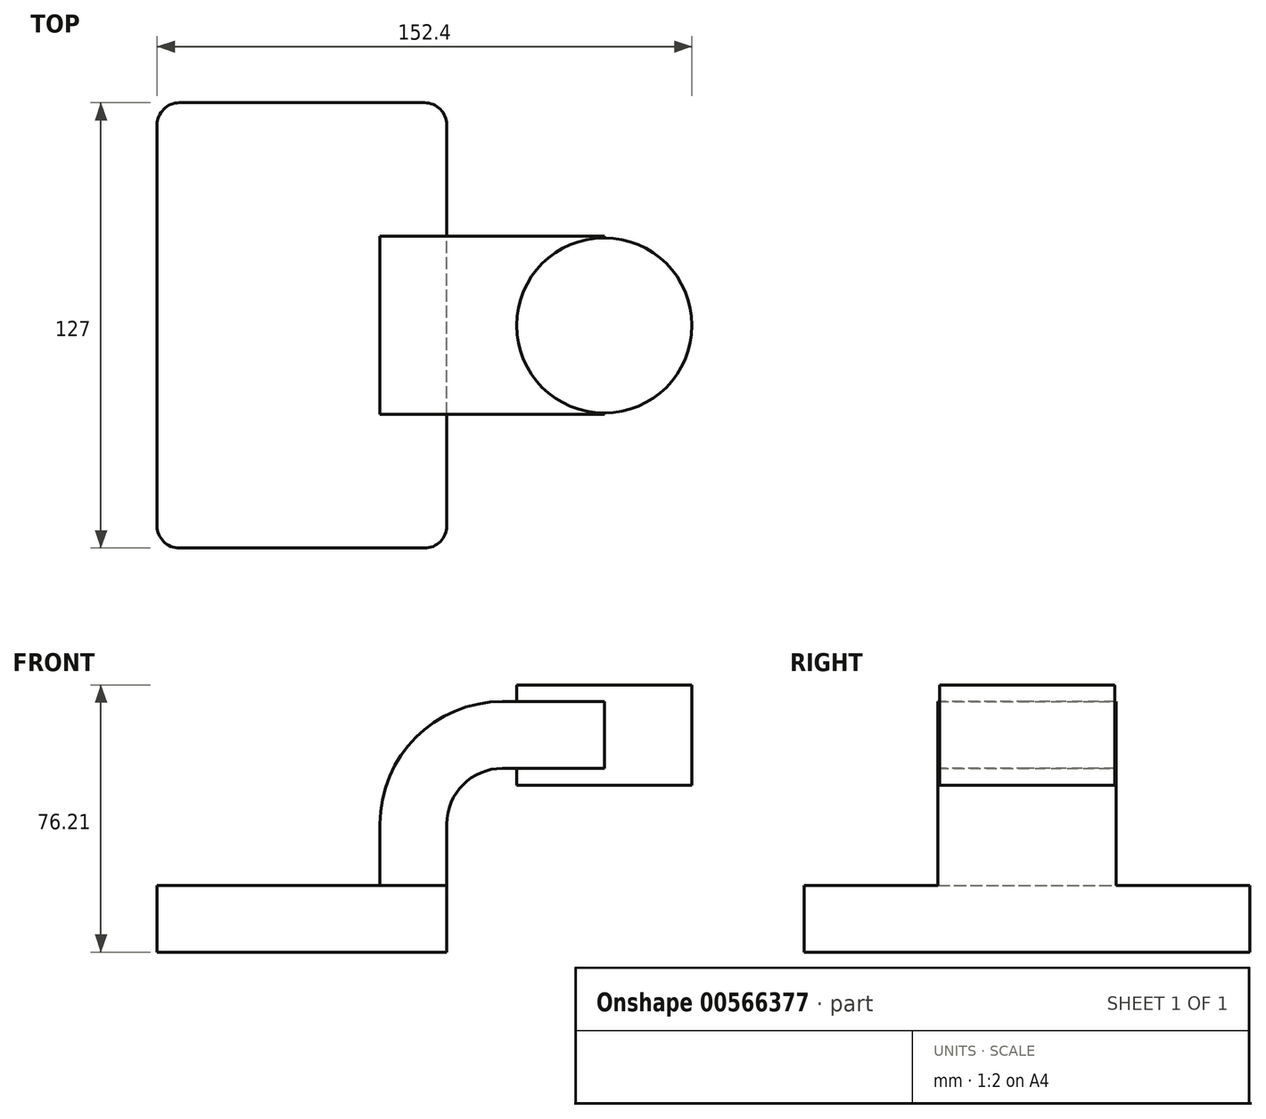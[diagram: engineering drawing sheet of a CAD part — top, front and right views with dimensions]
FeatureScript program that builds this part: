
annotation { "Feature Type Name" : "Feature", "Feature Type Description" : "" }
export const myFeature = defineFeature(function(context is Context, id is Id, definition is map)
    precondition{}
    {
        {
            var Q0;
            Q0=qCreatedBy(makeId("Front.planeOp"),FACE);
            var sketch = newSketch(context, id + "F0", { "sketchPlane" : qUnion([Q0])});
            skLineSegment(sketch, "E0.bottom", {"start": v(-41.28, 9.52) * mm, "end": v(41.28, 9.52) * mm});
            skLineSegment(sketch, "E0.top", {"start": v(-41.28, -9.52) * mm, "end": v(41.28, -9.52) * mm});
            skLineSegment(sketch, "E0.left", {"start": v(-41.28, 9.52) * mm, "end": v(-41.28, -9.52) * mm});
            skLineSegment(sketch, "E0.right", {"start": v(41.28, 9.52) * mm, "end": v(41.28, -9.52) * mm});
            skPoint(sketch, "E0.middle", {"position": v(0, 0) * mm});
            skLineSegment(sketch, "E1.bottom", {"start": v(60.32, 66.68) * mm, "end": v(111.12, 66.68) * mm});
            skLineSegment(sketch, "E1.top", {"start": v(60.32, 38.1) * mm, "end": v(111.12, 38.1) * mm});
            skLineSegment(sketch, "E1.left", {"start": v(60.32, 66.68) * mm, "end": v(60.32, 38.1) * mm});
            skLineSegment(sketch, "E1.right", {"start": v(111.12, 66.68) * mm, "end": v(111.12, 38.1) * mm});
            skPoint(sketch, "E1.middle", {"position": v(85.72, 52.39) * mm});
            skLineSegment(sketch, "E2", {"start": v(41.28, 9.52) * mm, "end": v(41.28, 27) * mm});
            skArc(sketch, "E3", {"start": v(41.28, 27) * mm, "mid": v(45.92, 38.23) * mm, "end": v(57.15, 42.88) * mm});
            skLineSegment(sketch, "E4", {"start": v(57.15, 42.88) * mm, "end": v(86.15, 42.88) * mm});
            skArc(sketch, "E5.0", {"start": v(22.23, 27) * mm, "mid": v(32.45, 51.7) * mm, "end": v(57.15, 61.93) * mm});
            skLineSegment(sketch, "E5.1", {"start": v(22.23, 9.52) * mm, "end": v(22.23, 27) * mm});
            skLineSegment(sketch, "E6", {"start": v(57.15, 61.93) * mm, "end": v(86.15, 61.93) * mm});
            skLineSegment(sketch, "E7", {"start": v(86.15, 38.1) * mm, "end": v(86.15, 66.68) * mm});
            skFitSpline(sketch, "E8", {"points": [v(-41.28, 9.52) * mm, v(57.15, 61.93) * mm], "startDerivative": vector(8.68, 121.34) * mm, "endDerivative": vector(149.27, -5.93) * mm});
            skSolve(sketch);
        }
        {
            var Q0;
            Q0=makeQuery(id+"F0.imprint","IMPRINT",FACE,{"disambiguationData":[TD([[makeQuery(id+"F0.imprint","IMPRINT",EDGE,{"derivedFrom":sQuery(id+"F0.wireOp",EDGE,"E0.top")}),1.0]])]});
            extrude(context, id + "F1", {"entities" : qUnion([Q0]), "endBound" : BoundingType.SYMMETRIC, "depth" : 127 * mm, "offsetDistance" : 25.4 * mm});
        }
        {
            var Q0;
            {var subQ1=sQuery(id+"F0.wireOp",EDGE,"E2");Q0=makeQuery(id+"F0.imprint","IMPRINT",FACE,{"disambiguationData":[TD([[makeQuery(id+"F0.imprint","IMPRINT",EDGE,{"derivedFrom":subQ1}),1.0]])]});}
            var Q1;
            {var subQ0=sQuery(id+"F0.wireOp",EDGE,"E6");var subQ1=sQuery(id+"F0.wireOp",EDGE,"E1.left");var subQ2=makeQuery(id+"F0.imprint","INTERSECT",VERTEX,{"derivedFrom":[subQ1,subQ0]});Q1=makeQuery(id+"F0.imprint","IMPRINT",FACE,{"disambiguationData":[TD([[makeQuery(id+"F0.imprint","IMPRINT",EDGE,{"disambiguationData":[TD([[subQ2,-1.0]])],"derivedFrom":subQ1}),1.0]])]});}
            extrude(context, id + "F2", {"entities" : qUnion([Q0, Q1]), "operationType" : NewBodyOperationType.ADD, "endBound" : BoundingType.SYMMETRIC, "depth" : 50.8 * mm, "offsetDistance" : 25.4 * mm});
        }
        {
            var Q0;
            Q0=makeQuery(id+"F0.imprint","IMPRINT",FACE,{"disambiguationData":[TD([[makeQuery(id+"F0.imprint","IMPRINT",EDGE,{"derivedFrom":sQuery(id+"F0.wireOp",EDGE,"E5.0")}),1.0]])]});
            extrude(context, id + "F3", {"entities" : qUnion([Q0]), "operationType" : NewBodyOperationType.ADD, "endBound" : BoundingType.SYMMETRIC, "depth" : 15.88 * mm, "offsetDistance" : 25.4 * mm});
        }
        {
            var Q0;
            {var subQ0=sQuery(id+"F0.wireOp",EDGE,"E1.right");Q0=makeQuery(id+"F0.imprint","IMPRINT",FACE,{"disambiguationData":[TD([[makeQuery(id+"F0.imprint","IMPRINT",EDGE,{"derivedFrom":subQ0}),-1.0]])]});}
            var Q1;
            Q1=sQuery(id+"F0.wireOp",EDGE,"E7");
            revolve(context, id + "F4", {"operationType" : NewBodyOperationType.ADD, "entities" : qUnion([Q0]), "axis" : qUnion([Q1]), "revolveType" : RevolveType.FULL});
        }
        {
            var Q0;
            Q0=makeQuery(id+"F1.opExtrude","CAP_EDGE",EDGE,{"disambiguationData":[OSD([sQuery(id+"F0.wireOp",EDGE,"E0.left")])],"isStart":false});
            var Q1;
            Q1=makeQuery(id+"F1.opExtrude","CAP_EDGE",EDGE,{"disambiguationData":[OSD([sQuery(id+"F0.wireOp",EDGE,"E0.right")])],"isStart":false});
            var Q2;
            Q2=makeQuery(id+"F1.opExtrude","CAP_EDGE",EDGE,{"disambiguationData":[OSD([sQuery(id+"F0.wireOp",EDGE,"E0.right")])],"isStart":true});
            var Q3;
            Q3=makeQuery(id+"F1.opExtrude","CAP_EDGE",EDGE,{"disambiguationData":[OSD([sQuery(id+"F0.wireOp",EDGE,"E0.left")])],"isStart":true});
            fillet(context, id + "F5", {"entities" : qUnion([Q0, Q1, Q2, Q3]), "radius" : 6.35 * mm, "tangentPropagation" : true, "allowEdgeOverflow" : false});
        }
    });
